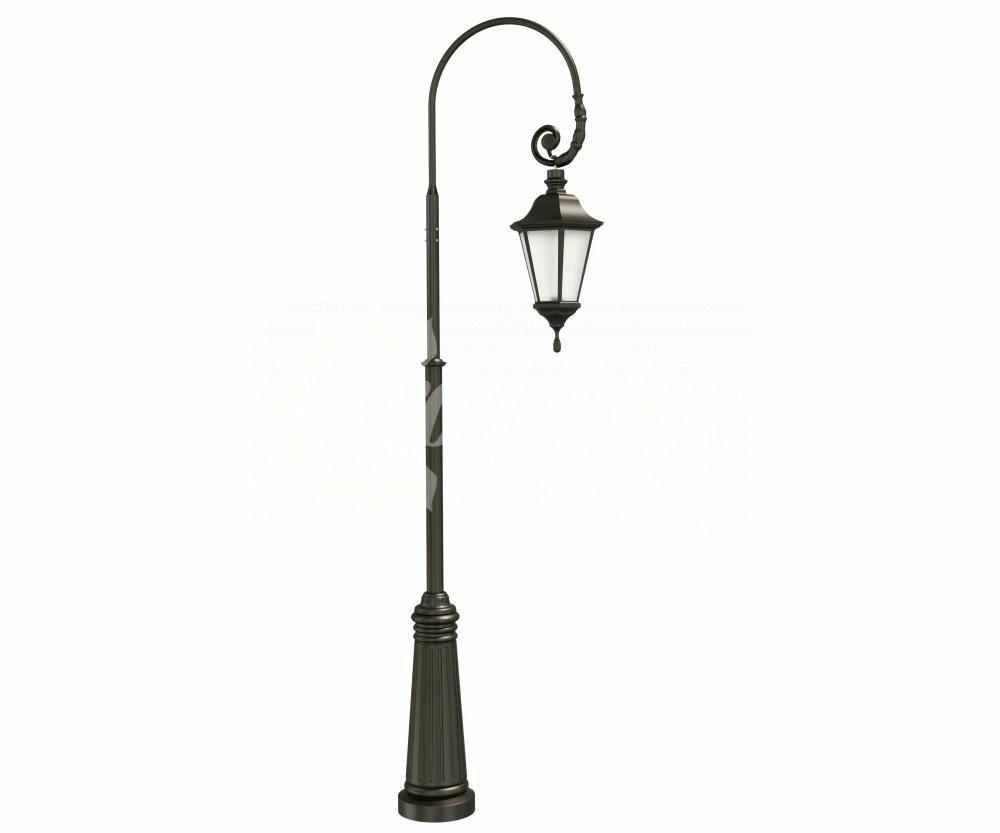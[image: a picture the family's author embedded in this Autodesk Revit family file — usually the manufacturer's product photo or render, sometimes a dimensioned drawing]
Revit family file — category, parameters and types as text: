
# Revit family: Фонарный столб Л-01 со светильником Арт 7431
name_source: partatom
category: Антураж
revit_build: Autodesk Revit 2018 (Build: 20180423_1000(x64)
units: mm (PartAtom-declared; Revit-internal decimal feet)

## family parameters
Всегда вертикально = Да
Источник визуального образа = Геометрия семейства
На основе рабочей плоскости = Нет
Общий = Нет
При загрузке вырезать с полостями = Нет
Точка расчета площади = Нет

## types (5) — shared parameters
URL = https://hobbyka.ru
Артикул товара = Арт. 7431
Группа модели = Светильники с чугунными опорами
Длина = 995 мм
Изготовитель = ООО «Хоббика»
Изображение типоразмера = Фонарный столб Л-01 со светильником Арт 7431.jpg
Материал изделия = Сталь, поликарбонат
Цвет основания = Сталь
Цвет столба = Нержавейка
Ширина = 525 мм

## per-type parameters (varying)
| type | Версия 3,516 м | Версия 4,016 м | Версия 4,516 м | Версия 5,016 м | Высота | Высота столба | Описание |
| Версия 3,516 м | Да | Нет | Нет | Нет | 3516 мм | 2426 мм | Фонарный столб Л-01 со светильником. Версия 3,516 м |
| Версия 4,016 м | Нет | Да | Нет | Нет | 4016 мм | 2926 мм | Фонарный столб Л-01 со светильником. Версия 4,016 м |
| Версия 4,516 м | Нет | Нет | Да | Нет | 4516 мм | 3426 мм | Фонарный столб Л-01 со светильником. Версия 4,516 м |
| Версия 5,016 м | Нет | Нет | Нет | Да | 5016 мм | 3926 мм | Фонарный столб Л-01 со светильником. Версия 5,016 м |
| Версия 5,516 м | Нет | Нет | Нет | Нет | 5516 мм | 4426 мм | Фонарный столб Л-01 со светильником. Версия 5,516 м |

## geometry (parser evidence)
native form markers: Blend x2
no freeform markers — native parametric forms only
